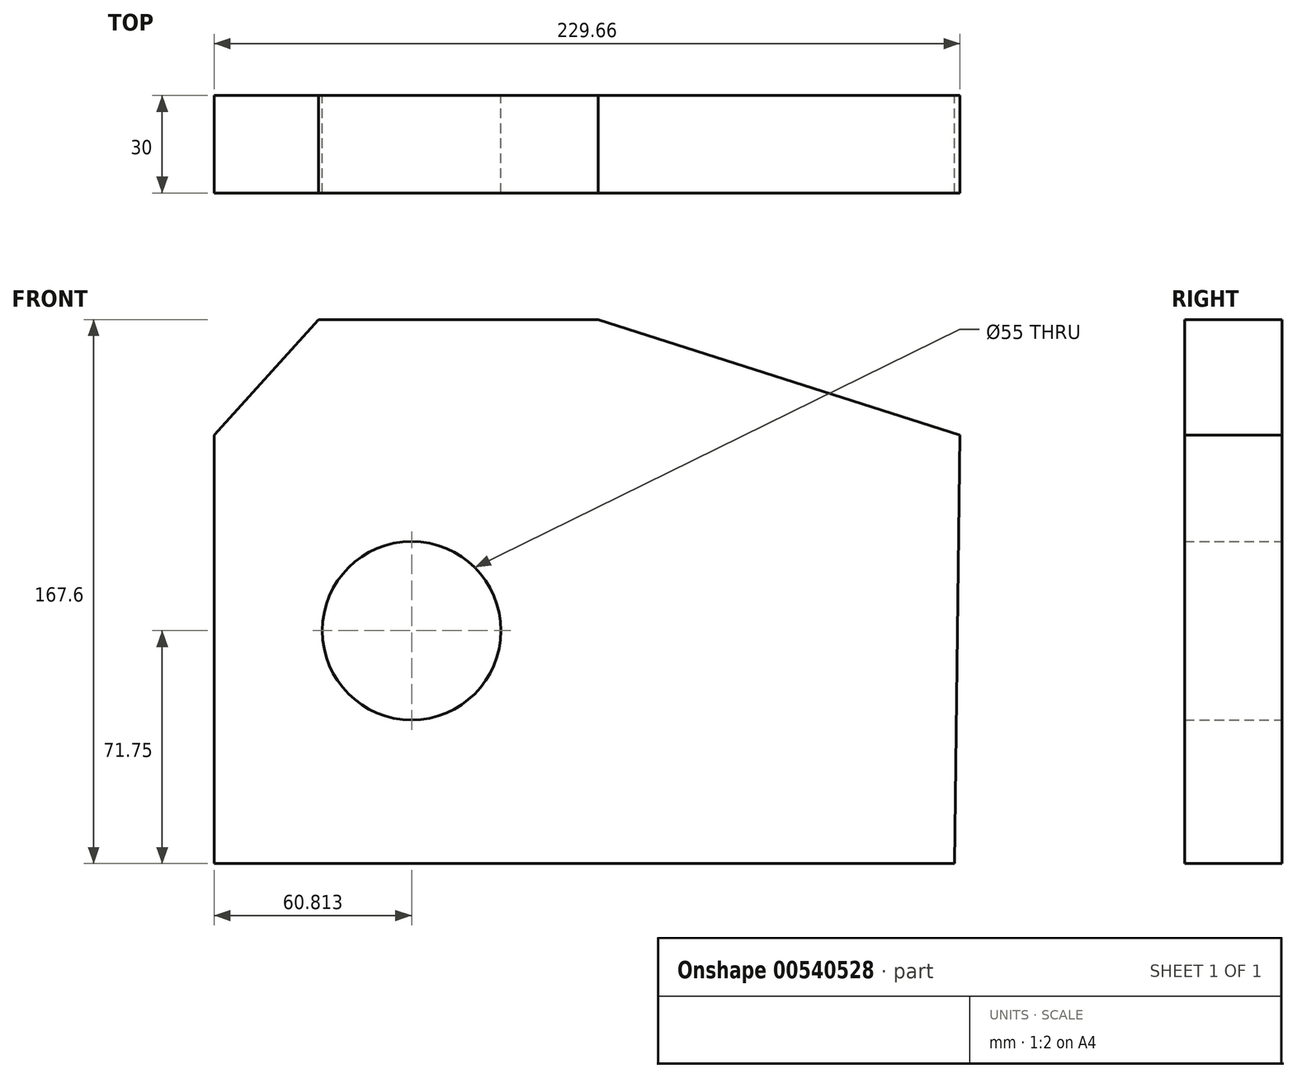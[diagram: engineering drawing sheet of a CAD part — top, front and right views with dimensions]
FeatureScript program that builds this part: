
annotation { "Feature Type Name" : "Feature", "Feature Type Description" : "" }
export const myFeature = defineFeature(function(context is Context, id is Id, definition is map)
    precondition{}
    {
        {
            var Q0;
            Q0=qCreatedBy(makeId("Front.planeOp"),FACE);
            var sketch = newSketch(context, id + "F0", { "sketchPlane" : qUnion([Q0])});
            skLineSegment(sketch, "E0", {"start": v(-112.44, -71.75) * mm, "end": v(-112.44, 3.25) * mm});
            skLineSegment(sketch, "E1", {"start": v(-112.44, 3.25) * mm, "end": v(-112.44, 60.25) * mm});
            skLineSegment(sketch, "E2", {"start": v(-112.44, 60.25) * mm, "end": v(-80.23, 95.85) * mm});
            skLineSegment(sketch, "E3", {"start": v(-80.23, 95.85) * mm, "end": v(5.77, 95.85) * mm});
            skLineSegment(sketch, "E4", {"start": v(5.77, 95.85) * mm, "end": v(117.22, 60.24) * mm});
            skLineSegment(sketch, "E5", {"start": v(-112.44, -71.75) * mm, "end": v(115.56, -71.75) * mm});
            skLineSegment(sketch, "E6", {"start": v(115.56, -71.75) * mm, "end": v(117.22, 60.24) * mm});
            skCircle(sketch, "E7", {"center": v(-51.63, 0) * mm, "radius": 27.5 * mm});
            skSolve(sketch);
        }
        {
            var Q0;
            Q0 = qSketchRegion(id + "F0", true);
            extrude(context, id + "F1", {"entities" : qUnion([Q0]), "depth" : 30 * mm, "offsetDistance" : 25 * mm});
        }
    });
